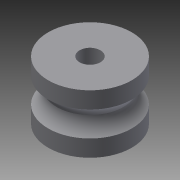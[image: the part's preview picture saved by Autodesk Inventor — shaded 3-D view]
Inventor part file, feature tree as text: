
AUTODESK INVENTOR PART (.ipt)
format: ipt  version: 2015 (Build 190159000, 159)  size: 122,368 bytes
history: native  units: mm
features: extrude x4, sketch x4, fillet x1
ambient origin geometry x8: Origin, YZ Plane, XZ Plane, XY Plane, X Axis, Y Axis, Z Axis, Center Point
bodies: Solid1 (feature_tree)
feature tree (9):
  extrude  "Extrusion1"  Depth=2.0mm TaperAngle=0.0deg
  extrude  "Extrusion2"  Depth=3.0mm TaperAngle=0.0deg
  extrude  "Extrusion3"  Depth=2.0mm
  fillet  "Fillet1"  Radius=2.5mm
  extrude  "Extrusion4"  [1 undecoded]
  sketch  "Sketch1"  dims[d0=10.0mm d1=2.0mm d2=0.0mm]
  sketch  "Sketch2"  dims[d3=8.0mm d4=3.0mm d5=0.0mm]
  sketch  "Sketch3"  dims[d6=2.0mm d7=0.0mm d8=2.0mm d9=2.5mm]
  sketch  "Sketch4"  dims[d10=20.0mm d11=0.0mm]
note: 1 required parameter value undecoded (feature->parameter linkage not recoverable at this tier; creation-order binding heuristic only, values carry confidence <= 0.55)
